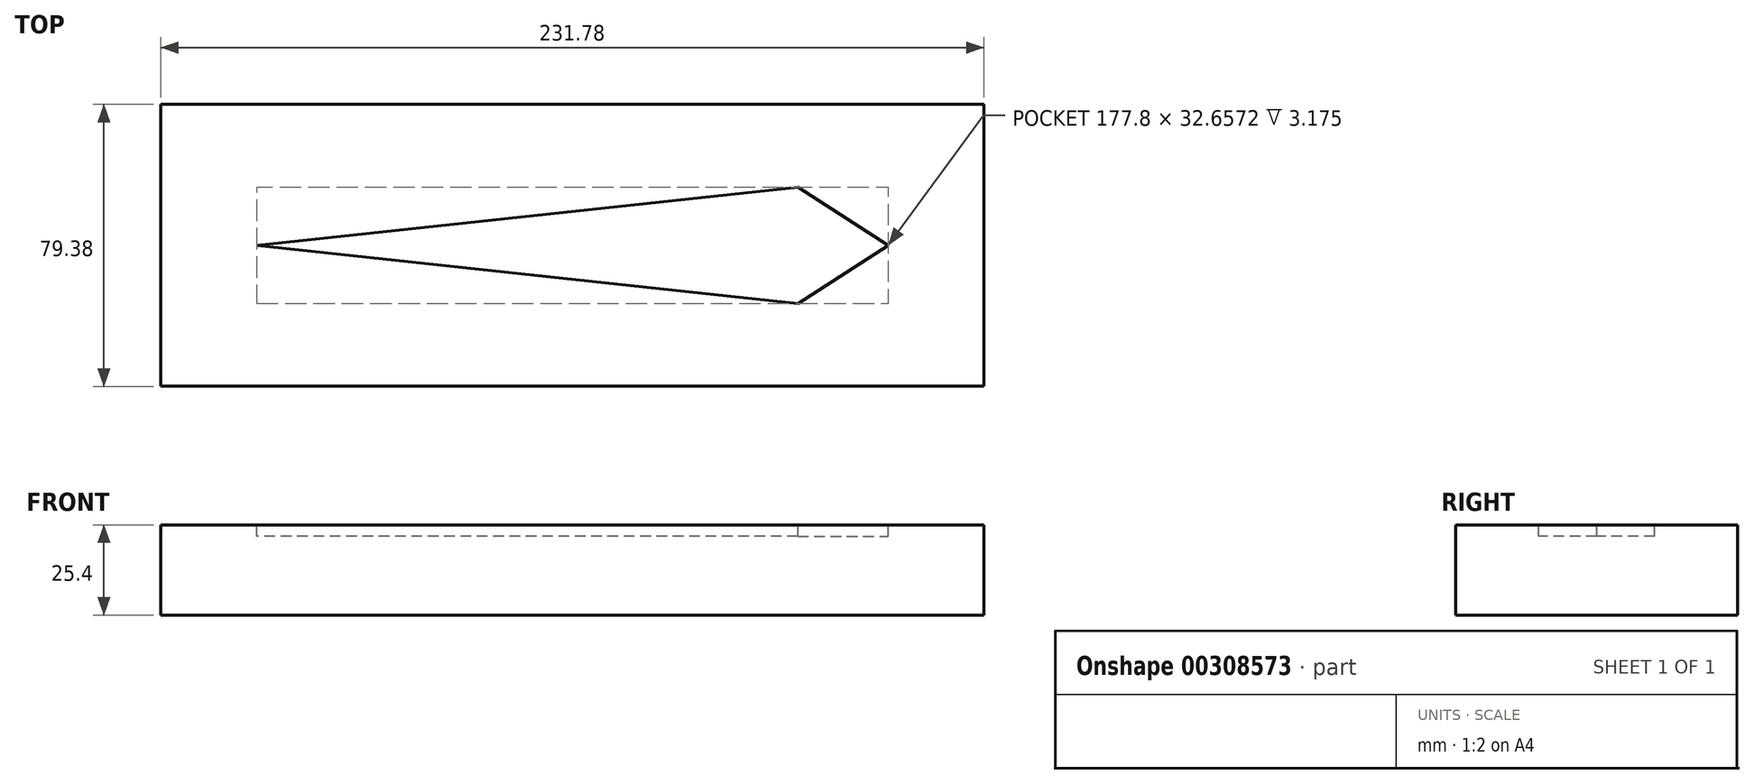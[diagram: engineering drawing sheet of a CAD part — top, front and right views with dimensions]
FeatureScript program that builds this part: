
annotation { "Feature Type Name" : "Feature", "Feature Type Description" : "" }
export const myFeature = defineFeature(function(context is Context, id is Id, definition is map)
    precondition{}
    {
        {
            var Q0;
            Q0=qCreatedBy(makeId("Top.planeOp"),FACE);
            var sketch = newSketch(context, id + "F0", { "sketchPlane" : qUnion([Q0])});
            skLineSegment(sketch, "E0.bottom", {"start": v(115.89, 39.69) * mm, "end": v(-115.89, 39.69) * mm});
            skLineSegment(sketch, "E0.top", {"start": v(115.89, -39.69) * mm, "end": v(-115.89, -39.69) * mm});
            skLineSegment(sketch, "E0.left", {"start": v(115.89, 39.69) * mm, "end": v(115.89, -39.69) * mm});
            skLineSegment(sketch, "E0.right", {"start": v(-115.89, 39.69) * mm, "end": v(-115.89, -39.69) * mm});
            skPoint(sketch, "E0.middle", {"position": v(0, 0) * mm});
            skSolve(sketch);
        }
        {
            var Q0;
            Q0 = qSketchRegion(id + "F0", true);
            extrude(context, id + "F1", {"entities" : qUnion([Q0]), "depth" : 25.4 * mm, "offsetDistance" : 25.4 * mm});
        }
        {
            var Q0;
            Q0=makeQuery(id+"F1.opExtrude","CAP_FACE",FACE,{"disambiguationData":[OSD([sQuery(id+"F0.wireOp",EDGE,"E0.bottom"),sQuery(id+"F0.wireOp",EDGE,"E0.top"),sQuery(id+"F0.wireOp",EDGE,"E0.left"),sQuery(id+"F0.wireOp",EDGE,"E0.right")])],"isStart":false});
            var sketch = newSketch(context, id + "F2", { "sketchPlane" : qUnion([Q0])});
            skLineSegment(sketch, "E1.bottom", {"start": v(-88.9, 19.05) * mm, "end": v(88.9, 19.05) * mm});
            skLineSegment(sketch, "E1.top", {"start": v(-88.9, -19.05) * mm, "end": v(88.9, -19.05) * mm});
            skLineSegment(sketch, "E1.left", {"start": v(-88.9, 19.05) * mm, "end": v(-88.9, -19.05) * mm});
            skLineSegment(sketch, "E1.right", {"start": v(88.9, 19.05) * mm, "end": v(88.9, -19.05) * mm});
            skLineSegment(sketch, "E2", {"start": v(88.9, 19.05) * mm, "end": v(-88.9, 0) * mm});
            skLineSegment(sketch, "E3", {"start": v(-88.9, 0) * mm, "end": v(88.9, -19.05) * mm});
            skLineSegment(sketch, "E4", {"start": v(63.5, 16.33) * mm, "end": v(88.9, 0) * mm});
            skLineSegment(sketch, "E5", {"start": v(88.9, 0) * mm, "end": v(63.5, -16.33) * mm});
            skLineSegment(sketch, "E6", {"start": v(0, 0) * mm, "end": v(-88.9, 0) * mm, "construction": true});
            skLineSegment(sketch, "E7", {"start": v(0, -0.96) * mm, "end": v(0, 19.05) * mm, "construction": true});
            skSolve(sketch);
        }
        {
            var Q0;
            {var subQ3=sQuery(id+"F2.wireOp",EDGE,"E4");Q0=makeQuery(id+"F2.imprint","IMPRINT",FACE,{"disambiguationData":[TD([[makeQuery(id+"F2.imprint","IMPRINT",EDGE,{"derivedFrom":subQ3}),-1.0]])]});}
            extrude(context, id + "F3", {"entities" : qUnion([Q0]), "operationType" : NewBodyOperationType.REMOVE, "oppositeDirection" : true, "depth" : 3.17 * mm, "offsetDistance" : 25.4 * mm});
        }
    });
